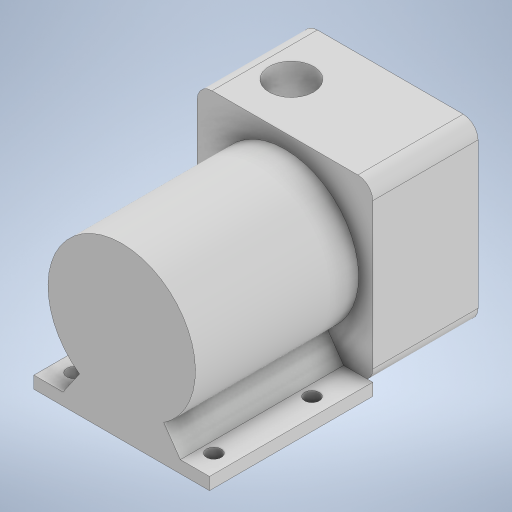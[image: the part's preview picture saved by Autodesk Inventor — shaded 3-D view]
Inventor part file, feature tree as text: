
AUTODESK INVENTOR PART (.ipt)
format: ipt  version: 2023 (Build 270158000, 158)  size: 287,232 bytes
history: native  units: mm
features: extrude x5, sketch x5, fillet x1
ambient origin geometry x8: Origin, YZ Plane, XZ Plane, XY Plane, X Axis, Y Axis, Z Axis, Center Point
bodies: Solid1 (feature_tree)
feature tree (11):
  extrude  "Extrusion1"  Depth=30.0mm TaperAngle=0.0deg
  extrude  "Extrusion2"  Depth=3.5mm
  extrude  "Extrusion3"  Depth=24.0mm
  extrude  "Extrusion4"  Depth=46.5mm
  extrude  "Extrusion5"  Depth=4.233333mm
  fillet  "Fillet1"  Radius=4.233333mm
  sketch  "Sketch1"  dims[d0=50.0mm d1=30.0mm d2=0.0mm]
  sketch  "Sketch2"  dims[d3=2.5mm d4=3.5mm]
  sketch  "Sketch3"  dims[d5=42.0mm d6=24.0mm]
  sketch  "Sketch4"  dims[d7=46.5mm d8=0.0mm d9=27.94mm]
  sketch  "Sketch5"  dims[d10=6.35mm d11=39.793333mm d12=4.233333mm d13=3.0mm d14=0.0mm d15=12.7mm d16=10.0mm d17=0.0mm d18=12.7mm d19=12.7mm d20=15.875mm d21=10.0mm d22=0.0mm d23=4.233333mm]
